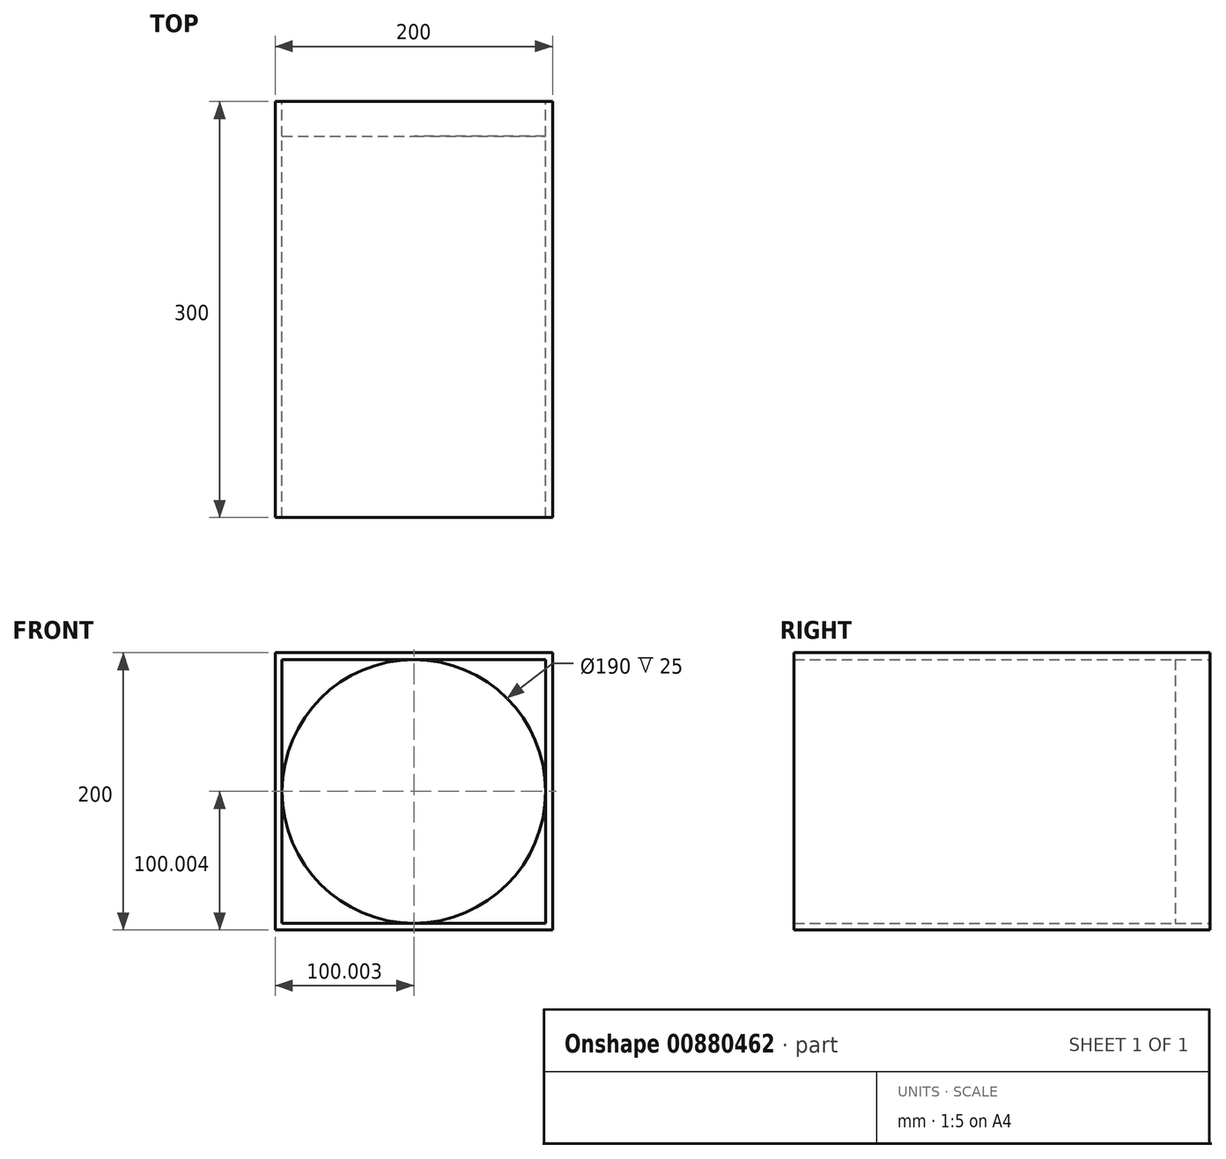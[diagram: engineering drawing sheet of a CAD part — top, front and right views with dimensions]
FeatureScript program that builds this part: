
annotation { "Feature Type Name" : "Feature", "Feature Type Description" : "" }
export const myFeature = defineFeature(function(context is Context, id is Id, definition is map)
    precondition{}
    {
        {
            var Q0;
            Q0=qCreatedBy(makeId("Front.planeOp"),FACE);
            var sketch = newSketch(context, id + "F0", { "sketchPlane" : qUnion([Q0])});
            skLineSegment(sketch, "E0.bottom", {"start": v(-114.65, 120.04) * mm, "end": v(85.35, 120.04) * mm});
            skLineSegment(sketch, "E0.top", {"start": v(-114.65, -79.96) * mm, "end": v(85.35, -79.96) * mm});
            skLineSegment(sketch, "E0.left", {"start": v(-114.65, 120.04) * mm, "end": v(-114.65, -79.96) * mm});
            skLineSegment(sketch, "E0.right", {"start": v(85.35, 120.04) * mm, "end": v(85.35, -79.96) * mm});
            skLineSegment(sketch, "E1.bottom", {"start": v(-109.65, 115.04) * mm, "end": v(80.35, 115.04) * mm});
            skLineSegment(sketch, "E1.top", {"start": v(-109.65, -74.96) * mm, "end": v(80.35, -74.96) * mm});
            skLineSegment(sketch, "E1.left", {"start": v(-109.65, 115.04) * mm, "end": v(-109.65, -74.96) * mm});
            skLineSegment(sketch, "E1.right", {"start": v(80.35, 115.04) * mm, "end": v(80.35, -74.96) * mm});
            skCircle(sketch, "E2", {"center": v(-14.65, 20.04) * mm, "radius": 95 * mm});
            skSolve(sketch);
        }
        {
            var Q0;
            {var subQ0=sQuery(id+"F0.wireOp",EDGE,"E1.right");var subQ1=sQuery(id+"F0.wireOp",EDGE,"E1.bottom");var subQ2=makeQuery(id+"F0.imprint","INTERSECT",VERTEX,{"derivedFrom":[subQ1,subQ0]});Q0=makeQuery(id+"F0.imprint","IMPRINT",FACE,{"disambiguationData":[TD([[makeQuery(id+"F0.imprint","IMPRINT",EDGE,{"disambiguationData":[TD([[subQ2,1.0]])],"derivedFrom":subQ1}),-1.0]])]});}
            var Q1;
            {var subQ0=sQuery(id+"F0.wireOp",EDGE,"E1.left");var subQ1=sQuery(id+"F0.wireOp",EDGE,"E1.bottom");var subQ2=makeQuery(id+"F0.imprint","INTERSECT",VERTEX,{"derivedFrom":[subQ1,subQ0]});Q1=makeQuery(id+"F0.imprint","IMPRINT",FACE,{"disambiguationData":[TD([[makeQuery(id+"F0.imprint","IMPRINT",EDGE,{"disambiguationData":[TD([[subQ2,-1.0]])],"derivedFrom":subQ1}),-1.0]])]});}
            var Q2;
            {var subQ0=sQuery(id+"F0.wireOp",EDGE,"E1.left");var subQ1=sQuery(id+"F0.wireOp",EDGE,"E1.top");var subQ2=makeQuery(id+"F0.imprint","INTERSECT",VERTEX,{"derivedFrom":[subQ1,subQ0]});Q2=makeQuery(id+"F0.imprint","IMPRINT",FACE,{"disambiguationData":[TD([[makeQuery(id+"F0.imprint","IMPRINT",EDGE,{"disambiguationData":[TD([[subQ2,-1.0]])],"derivedFrom":subQ1}),1.0]])]});}
            var Q3;
            {var subQ0=sQuery(id+"F0.wireOp",EDGE,"E1.right");var subQ1=sQuery(id+"F0.wireOp",EDGE,"E1.top");var subQ2=makeQuery(id+"F0.imprint","INTERSECT",VERTEX,{"derivedFrom":[subQ1,subQ0]});Q3=makeQuery(id+"F0.imprint","IMPRINT",FACE,{"disambiguationData":[TD([[makeQuery(id+"F0.imprint","IMPRINT",EDGE,{"disambiguationData":[TD([[subQ2,1.0]])],"derivedFrom":subQ1}),1.0]])]});}
            extrude(context, id + "F1", {"entities" : qUnion([Q0, Q1, Q2, Q3]), "depth" : 25 * mm, "offsetDistance" : 25 * mm});
        }
        {
            var Q0;
            Q0=makeQuery(id+"F0.imprint","IMPRINT",FACE,{"disambiguationData":[TD([[makeQuery(id+"F0.imprint","IMPRINT",EDGE,{"derivedFrom":sQuery(id+"F0.wireOp",EDGE,"E0.bottom")}),-1.0]])]});
            extrude(context, id + "F2", {"entities" : qUnion([Q0]), "depth" : 25 * mm, "offsetDistance" : 25 * mm});
        }
        {
            var Q0;
            Q0=makeQuery(id+"F2.opExtrude","CAP_FACE",FACE,{"disambiguationData":[OSD([sQuery(id+"F0.wireOp",EDGE,"E0.bottom"),sQuery(id+"F0.wireOp",EDGE,"E0.top"),sQuery(id+"F0.wireOp",EDGE,"E0.left"),sQuery(id+"F0.wireOp",EDGE,"E0.right"),sQuery(id+"F0.wireOp",EDGE,"E1.bottom"),sQuery(id+"F0.wireOp",EDGE,"E1.top"),sQuery(id+"F0.wireOp",EDGE,"E1.left"),sQuery(id+"F0.wireOp",EDGE,"E1.right")])],"isStart":false});
            extrude(context, id + "F3", {"entities" : qUnion([Q0]), "operationType" : NewBodyOperationType.ADD, "depth" : 275 * mm, "offsetDistance" : 25 * mm});
        }
    });
